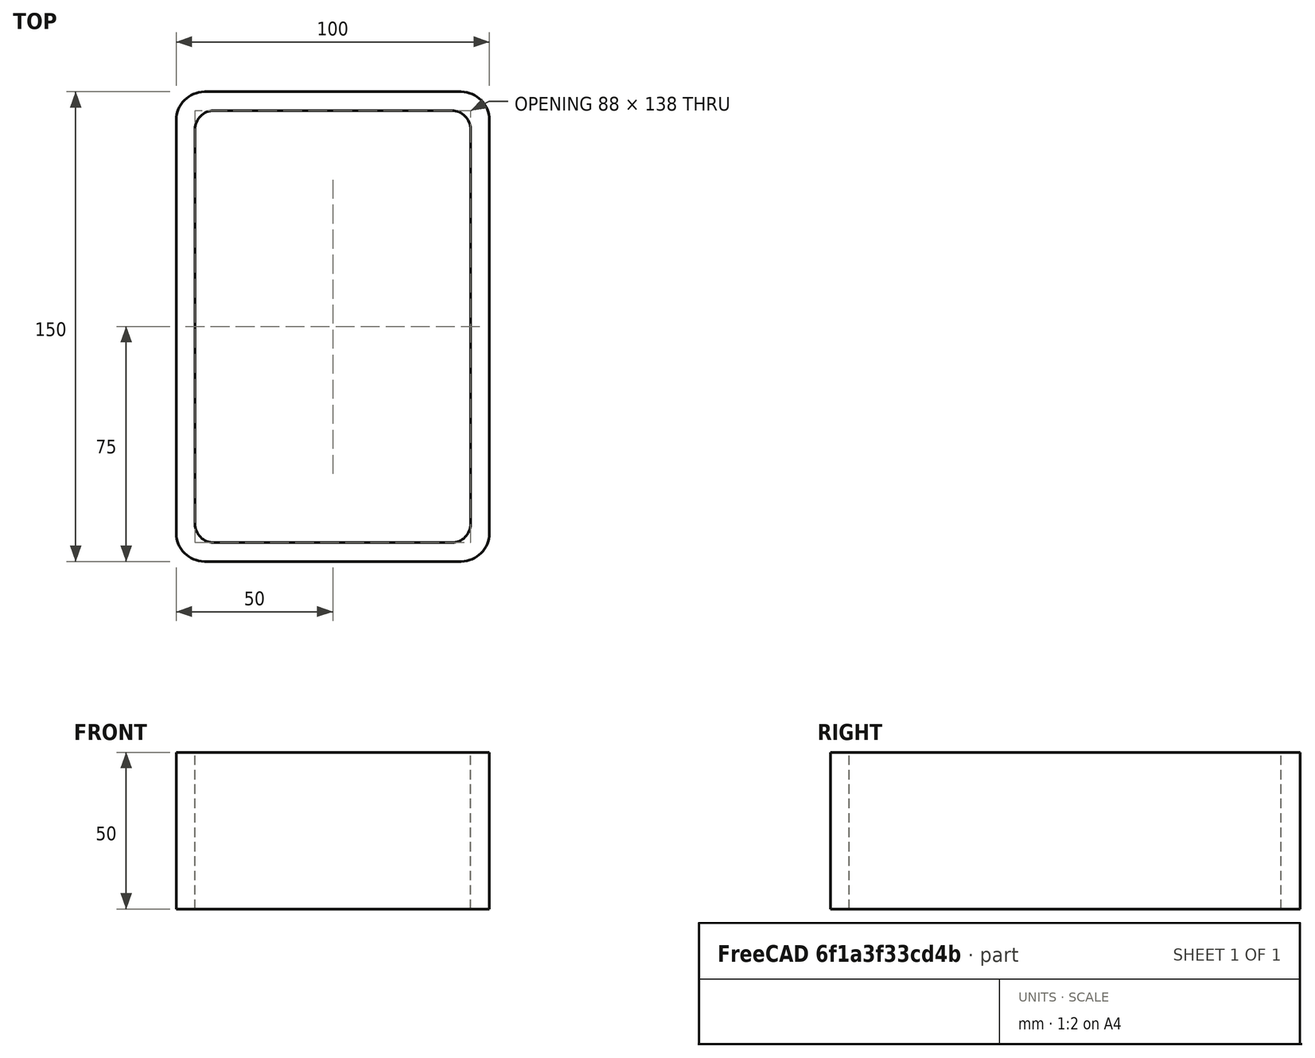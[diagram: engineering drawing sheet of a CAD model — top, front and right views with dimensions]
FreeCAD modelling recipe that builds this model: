
FCSTD DOCUMENT  (FreeCAD 0.15R4671 (Git))
Label: Rectangular hollow section 150x100x6 EN10219 S235JRH
License: All rights reserved
LicenseURL: http://en.wikipedia.org/wiki/All_rights_reserved
objects: Sketcher::SketchObject×1, Part::Extrusion×1
note: 2 computed .brp shape members not serialized (recipe doc carries the construction recipe); baked Part::Feature solids carry a one-line shape summary decoded from their .brp

FEATURE [Sketcher::SketchObject] Sketch
  sketch-geometry (16):
    g0: LineSegment StartX=-38 StartY=69 StartZ=0 EndX=38 EndY=69 EndZ=0
    g1: LineSegment StartX=44 StartY=63 StartZ=0 EndX=44 EndY=-63 EndZ=0
    g2: LineSegment StartX=38 StartY=-69 StartZ=0 EndX=-38 EndY=-69 EndZ=0
    g3: LineSegment StartX=-44 StartY=-63 StartZ=0 EndX=-44 EndY=63 EndZ=0
    g4: LineSegment StartX=-41 StartY=75 StartZ=0 EndX=41 EndY=75 EndZ=0
    g5: LineSegment StartX=50 StartY=66 StartZ=0 EndX=50 EndY=-66 EndZ=0
    g6: LineSegment StartX=41 StartY=-75 StartZ=0 EndX=-41 EndY=-75 EndZ=0
    g7: LineSegment StartX=-50 StartY=-66 StartZ=0 EndX=-50 EndY=66 EndZ=0
    g8: ArcOfCircle CenterX=-38 CenterY=63 CenterZ=0 NormalX=0 NormalY=0 NormalZ=1 Radius=6 StartAngle=1.5708 EndAngle=3.14159
    g9: ArcOfCircle CenterX=38 CenterY=63 CenterZ=0 NormalX=0 NormalY=0 NormalZ=1 Radius=6 StartAngle=0 EndAngle=1.5708
    g10: ArcOfCircle CenterX=38 CenterY=-63 CenterZ=0 NormalX=0 NormalY=0 NormalZ=1 Radius=6 StartAngle=4.71239 EndAngle=6.28319
    g11: ArcOfCircle CenterX=-38 CenterY=-63 CenterZ=0 NormalX=0 NormalY=0 NormalZ=1 Radius=6 StartAngle=3.14159 EndAngle=4.71239
    g12: ArcOfCircle CenterX=41 CenterY=66 CenterZ=0 NormalX=0 NormalY=0 NormalZ=1 Radius=9 StartAngle=0 EndAngle=1.5708
    g13: ArcOfCircle CenterX=41 CenterY=-66 CenterZ=0 NormalX=0 NormalY=0 NormalZ=1 Radius=9 StartAngle=4.71239 EndAngle=6.28319
    g14: ArcOfCircle CenterX=-41 CenterY=-66 CenterZ=0 NormalX=0 NormalY=0 NormalZ=1 Radius=9 StartAngle=3.14159 EndAngle=4.71239
    g15: ArcOfCircle CenterX=-41 CenterY=66 CenterZ=0 NormalX=0 NormalY=0 NormalZ=1 Radius=9 StartAngle=1.5708 EndAngle=3.14159
  constraints (36):
    c: Horizontal(g2)
    c: Vertical(g3)
    c: Horizontal(g6)
    c: Vertical(g7)
    c: Tangent(g3,g8) = 1.5708
    c: Tangent(g0,g8) = 1.5708
    c: Tangent(g0,g9) = 1.5708
    c: Tangent(g1,g9) = 1.5708
    c: Tangent(g1,g10) = 1.5708
    c: Tangent(g2,g10) = 1.5708
    c: Tangent(g2,g11) = 1.5708
    c: Tangent(g3,g11) = 1.5708
    c: Tangent(g4,g12) = 1.5708
    c: Tangent(g5,g12) = 1.5708
    c: Tangent(g5,g13) = 1.5708
    c: Tangent(g6,g13) = 1.5708
    c: Tangent(g6,g14) = 1.5708
    c: Tangent(g7,g14) = 1.5708
    c: Tangent(g7,g15) = 1.5708
    c: Tangent(g4,g15) = 1.5708
    c: Equal(g9,g8)
    c: Equal(g9,g11)
    c: Equal(g9,g10)
    c: Equal(g12,g15)
    c: Equal(g12,g14)
    c: Equal(g12,g13)
    c: Symmetric(g4,g6,g-1)
    c: Symmetric(g7,g5,g-2)
    c: DistanceY(g4,g6) = -150
    c: DistanceX(g7,g5) = 100
    c: Symmetric(g3,g1,g-2)
    c: Symmetric(g0,g2,g-1)
    c: DistanceY(g0,g4) = 6
    c: DistanceX(g5,g1) = -6
    c: Radius(g9) = 6
    c: Radius(g12) = 9
FEATURE [Part::Extrusion] Extrude  label="Rectangular hollow section 150x100x6 EN10219 S235JRH"
  Base = -> Sketch
  Dir = (0,0,50)
  Solid = true
